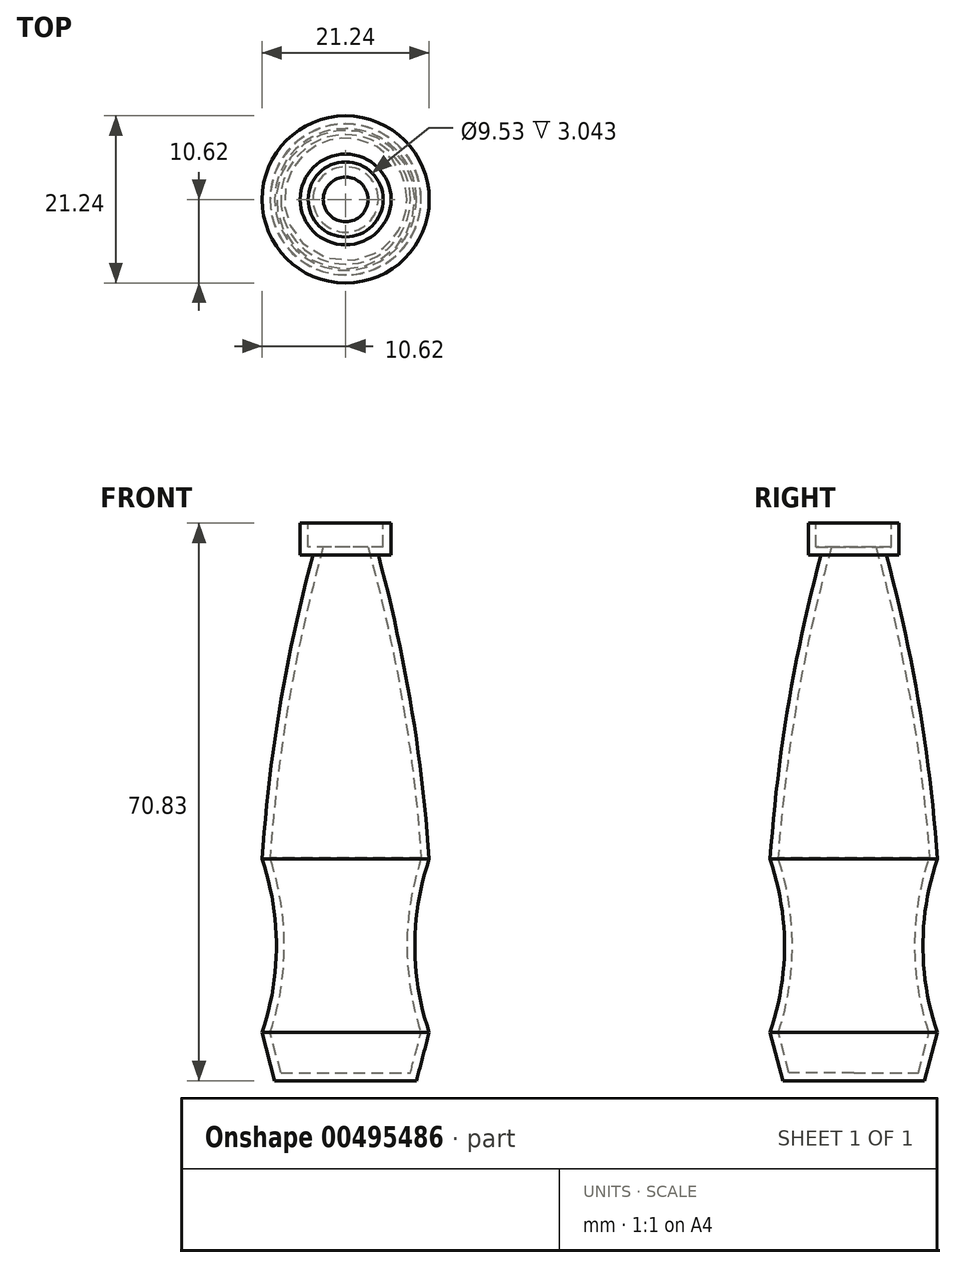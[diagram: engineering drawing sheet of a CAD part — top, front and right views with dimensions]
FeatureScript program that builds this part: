
annotation { "Feature Type Name" : "Feature", "Feature Type Description" : "" }
export const myFeature = defineFeature(function(context is Context, id is Id, definition is map)
    precondition{}
    {
        {
            var Q0;
            Q0=qCreatedBy(makeId("Front.planeOp"),FACE);
            var sketch = newSketch(context, id + "F0", { "sketchPlane" : qUnion([Q0])});
            skPoint(sketch, "E0.start.orphan", {"position": v(42.4, 65) * mm});
            skPoint(sketch, "E1.start.orphan", {"position": v(34.33, 65) * mm});
            skLineSegment(sketch, "E2", {"start": v(10.62, 9.96) * mm, "end": v(10.62, 9.96) * mm});
            skArc(sketch, "E3", {"start": v(10.62, 31.95) * mm, "mid": v(8.8, 20.95) * mm, "end": v(10.62, 9.96) * mm});
            skArc(sketch, "E4", {"start": v(10.62, 31.95) * mm, "mid": v(8.32, 51.43) * mm, "end": v(4.15, 70.6) * mm});
            skLineSegment(sketch, "E5", {"start": v(4.15, 70.6) * mm, "end": v(5.77, 70.6) * mm});
            skLineSegment(sketch, "E6", {"start": v(5.77, 70.6) * mm, "end": v(5.77, 74.64) * mm});
            skLineSegment(sketch, "E7", {"start": v(10.62, 9.96) * mm, "end": v(9, 3.81) * mm});
            skLineSegment(sketch, "E8", {"start": v(9, 3.81) * mm, "end": v(0, 3.81) * mm});
            skLineSegment(sketch, "E9", {"start": v(5.77, 74.64) * mm, "end": v(0, 74.64) * mm});
            skLineSegment(sketch, "E10", {"start": v(0, 74.64) * mm, "end": v(0, 3.81) * mm});
            skSolve(sketch);
        }
        {
            var Q0;
            Q0=makeQuery(id+"F0.imprint","IMPRINT",FACE,{"disambiguationData":[TD([[makeQuery(id+"F0.imprint","IMPRINT",EDGE,{"derivedFrom":sQuery(id+"F0.wireOp",EDGE,"E3")}),-1.0]])]});
            var Q1;
            Q1=sQuery(id+"F0.wireOp",EDGE,"E10");
            revolve(context, id + "F1", {"entities" : qUnion([Q0]), "axis" : qUnion([Q1]), "revolveType" : RevolveType.FULL});
        }
        {
            var Q0;
            Q0=makeQuery(id+"F1.opRevolve","SWEPT_FACE",FACE,{"disambiguationData":[OSD([sQuery(id+"F0.wireOp",EDGE,"E9")])]});
            shell(context, id + "F2", {"entities" : qUnion([Q0]), "thickness" : 1 * mm});
        }
    });
